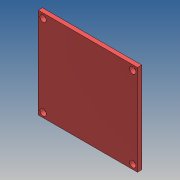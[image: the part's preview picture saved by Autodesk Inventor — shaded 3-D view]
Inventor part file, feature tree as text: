
AUTODESK INVENTOR PART (.ipt)
format: ipt  version: 2017 (Build 210142000, 142)  size: 88,576 bytes
history: native  units: mm
features: other x1, extrude x1, sketch x1
ambient origin geometry x8: Origin, YZ Plane, XZ Plane, XY Plane, X Axis, Y Axis, Z Axis, Center Point
bodies: Body1 (feature_tree)
feature tree (3):
  other  "Sólido1"
  extrude  "Extrusión1"  Depth=2.0mm
  sketch  "Boceto1"  dims[d0=3.0mm d1=2.25mm d2=43.0mm d3=47.0mm d4=2.0mm d5=0.0mm d6=38.5mm d7=42.5mm]
